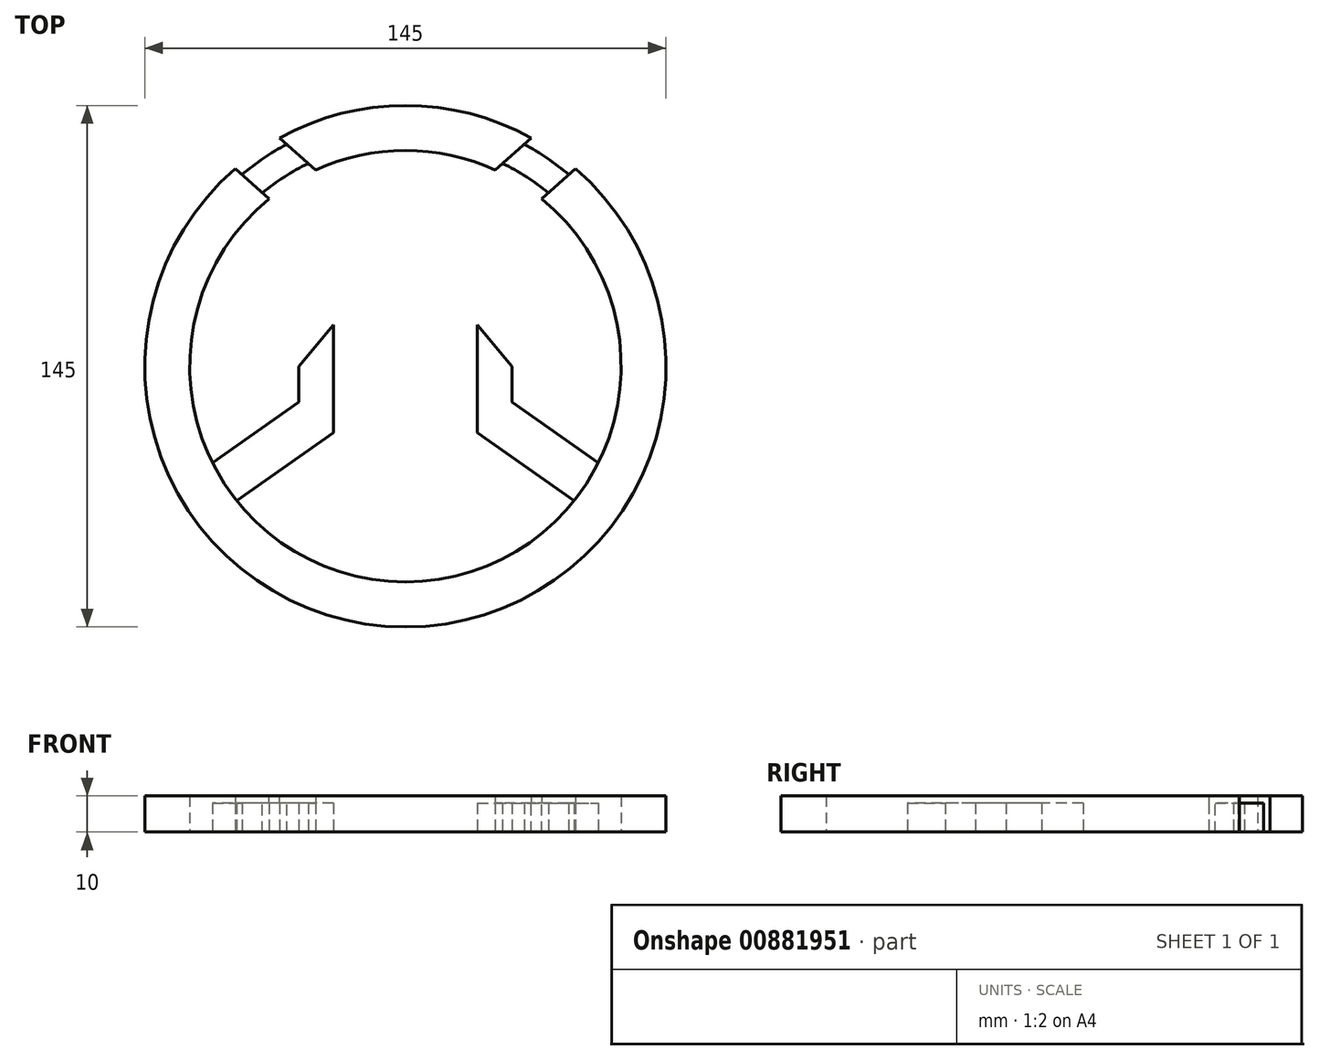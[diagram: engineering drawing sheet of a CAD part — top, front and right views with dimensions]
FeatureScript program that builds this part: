
annotation { "Feature Type Name" : "Feature", "Feature Type Description" : "" }
export const myFeature = defineFeature(function(context is Context, id is Id, definition is map)
    precondition{}
    {
        {
            var Q0;
            Q0=qCreatedBy(makeId("Top.planeOp"),FACE);
            var sketch = newSketch(context, id + "F0", { "sketchPlane" : qUnion([Q0])});
            skCircle(sketch, "E0", {"center": v(0, 0) * mm, "radius": 14 * mm});
            skArc(sketch, "E1", {"start": v(-20, -10.3) * mm, "mid": v(0, -22.5) * mm, "end": v(20, -10.3) * mm});
            skArc(sketch, "E2.MirrorC", {"start": v(20, -10.3) * mm, "mid": v(0, -22.5) * mm, "end": v(-20, -10.3) * mm});
            skLineSegment(sketch, "E3.right", {"start": v(-20, 11.5) * mm, "end": v(-20, -18.5) * mm});
            skPoint(sketch, "E4.orphan", {"position": v(0, 39.65) * mm});
            skLineSegment(sketch, "E5", {"start": v(-20, 11.5) * mm, "end": v(-29.64, 0) * mm});
            skLineSegment(sketch, "E6", {"start": v(-29.64, 0) * mm, "end": v(-29.64, -10) * mm});
            skLineSegment(sketch, "E7", {"start": v(-20, -18.5) * mm, "end": v(-46.94, -37.37) * mm});
            skLineSegment(sketch, "E8", {"start": v(-29.64, -10) * mm, "end": v(-53.67, -26.82) * mm});
            skArc(sketch, "E9", {"start": v(-46.94, -37.37) * mm, "mid": v(-26.05, -54.05) * mm, "end": v(0, -60) * mm});
            skArc(sketch, "E10", {"start": v(0, 72.5) * mm, "mid": v(-18.07, 70.21) * mm, "end": v(-35, 63.5) * mm});
            skArc(sketch, "E11.trimOffspring", {"start": v(0, 60) * mm, "mid": v(-12.8, 58.62) * mm, "end": v(-25, 54.54) * mm});
            skLineSegment(sketch, "E12.trimOffspring", {"start": v(0, 20) * mm, "end": v(0, 14) * mm});
            skLineSegment(sketch, "E13.trimOffspring", {"start": v(0, -14) * mm, "end": v(0, -20) * mm});
            skArc(sketch, "E14.MirrorCS", {"start": v(0, 72.5) * mm, "mid": v(18.07, 70.21) * mm, "end": v(35, 63.5) * mm});
            skArc(sketch, "E15.MirrorCS", {"start": v(0, 60) * mm, "mid": v(12.8, 58.62) * mm, "end": v(25, 54.54) * mm});
            skArc(sketch, "E16.MirrorCS", {"start": v(46.94, -37.37) * mm, "mid": v(26.05, -54.05) * mm, "end": v(0, -60) * mm});
            skLineSegment(sketch, "E17.MirrorCS", {"start": v(20, -18.5) * mm, "end": v(46.94, -37.37) * mm});
            skLineSegment(sketch, "E18.MirrorCS", {"start": v(29.64, -10) * mm, "end": v(53.67, -26.82) * mm});
            skLineSegment(sketch, "E19.MirrorCS", {"start": v(29.64, 0) * mm, "end": v(29.64, -10) * mm});
            skLineSegment(sketch, "E20.MirrorCS", {"start": v(20, 11.5) * mm, "end": v(29.64, 0) * mm});
            skLineSegment(sketch, "E21.MirrorCS", {"start": v(20, 11.5) * mm, "end": v(20, -18.5) * mm});
            skLineSegment(sketch, "E22", {"start": v(-35, 63.5) * mm, "end": v(-33.02, 61.72) * mm});
            skLineSegment(sketch, "E23.MirrorCS", {"start": v(35, 63.5) * mm, "end": v(33.02, 61.72) * mm});
            skLineSegment(sketch, "E24", {"start": v(-47.32, 54.93) * mm, "end": v(-45.44, 53.25) * mm});
            skLineSegment(sketch, "E25.MirrorCS", {"start": v(47.32, 54.93) * mm, "end": v(45.44, 53.25) * mm});
            skArc(sketch, "E26.trimOffspring", {"start": v(-47.32, 54.93) * mm, "mid": v(-67.97, -25.24) * mm, "end": v(0, -72.5) * mm});
            skArc(sketch, "E27.trimOffspring", {"start": v(-37.9, 46.5) * mm, "mid": v(-58.66, 12.6) * mm, "end": v(-53.67, -26.82) * mm});
            skArc(sketch, "E28.trimOffspring", {"start": v(37.9, 46.5) * mm, "mid": v(58.66, 12.6) * mm, "end": v(53.67, -26.82) * mm});
            skArc(sketch, "E29.trimOffspring", {"start": v(47.32, 54.93) * mm, "mid": v(67.97, -25.24) * mm, "end": v(0, -72.5) * mm});
            skArc(sketch, "E30", {"start": v(-27.02, 56.36) * mm, "mid": v(-33.66, 52.66) * mm, "end": v(-39.8, 48.2) * mm});
            skArc(sketch, "E31", {"start": v(-33.02, 61.72) * mm, "mid": v(-39.46, 57.82) * mm, "end": v(-45.44, 53.25) * mm});
            skArc(sketch, "E32.trimOffspring", {"start": v(45.44, 53.25) * mm, "mid": v(39.46, 57.82) * mm, "end": v(33.02, 61.72) * mm});
            skArc(sketch, "E33.trimOffspring", {"start": v(39.8, 48.2) * mm, "mid": v(33.66, 52.66) * mm, "end": v(27.02, 56.36) * mm});
            skLineSegment(sketch, "E34.trimOffspring", {"start": v(39.8, 48.2) * mm, "end": v(37.9, 46.5) * mm});
            skLineSegment(sketch, "E35.trimOffspring", {"start": v(27.02, 56.36) * mm, "end": v(25, 54.54) * mm});
            skLineSegment(sketch, "E36.trimOffspring", {"start": v(-27.02, 56.36) * mm, "end": v(-25, 54.54) * mm});
            skLineSegment(sketch, "E37.trimOffspring", {"start": v(-39.8, 48.2) * mm, "end": v(-37.9, 46.5) * mm});
            skArc(sketch, "E38.trimOffspring", {"start": v(20, 10.3) * mm, "mid": v(0, 22.5) * mm, "end": v(-20, 10.3) * mm});
            skArc(sketch, "E39.trimOffspring", {"start": v(-20, 10.3) * mm, "mid": v(0, 22.5) * mm, "end": v(20, 10.3) * mm});
            skSolve(sketch);
        }
        {
            var Q0;
            Q0 = qSketchRegion(id + "F0", true);
            var Q1;
            {var subQ3=sQuery(id+"F0.wireOp",EDGE,"E12.trimOffspring");Q1=makeQuery(id+"F0.imprint","IMPRINT",FACE,{"disambiguationData":[TD([[makeQuery(id+"F0.imprint","IMPRINT",EDGE,{"derivedFrom":subQ3}),-1.0]])]});}
            var Q2;
            {var subQ0=sQuery(id+"F0.wireOp",EDGE,"E12.trimOffspring");Q2=makeQuery(id+"F0.imprint","IMPRINT",FACE,{"disambiguationData":[TD([[makeQuery(id+"F0.imprint","IMPRINT",EDGE,{"derivedFrom":subQ0}),1.0]])]});}
            var Q3;
            {var subQ1=sQuery(id+"F0.wireOp",EDGE,"E2.MirrorC");Q3=makeQuery(id+"F0.imprint","IMPRINT",FACE,{"disambiguationData":[TD([[makeQuery(id+"F0.imprint","IMPRINT",EDGE,{"derivedFrom":subQ1}),-1.0]])]});}
            extrude(context, id + "F1", {"entities" : qUnion([Q0, Q1, Q2, Q3]), "depth" : 8 * mm, "offsetDistance" : 25 * mm});
        }
        {
            var Q0;
            Q0=qCreatedBy(makeId("Top.planeOp"),FACE);
            var sketch = newSketch(context, id + "F2", { "sketchPlane" : qUnion([Q0])});
            skArc(sketch, "E40", {"start": v(-37.9, 46.51) * mm, "mid": v(0, -60) * mm, "end": v(37.9, 46.51) * mm});
            skArc(sketch, "E41", {"start": v(-47.33, 54.92) * mm, "mid": v(0, -72.5) * mm, "end": v(47.33, 54.92) * mm});
            skLineSegment(sketch, "E42", {"start": v(-47.33, 54.92) * mm, "end": v(-37.9, 46.51) * mm});
            skLineSegment(sketch, "E43", {"start": v(-35, 63.5) * mm, "end": v(-24.99, 54.55) * mm});
            skLineSegment(sketch, "E44.MirrorCS", {"start": v(35, 63.5) * mm, "end": v(24.99, 54.55) * mm});
            skLineSegment(sketch, "E45.MirrorCS", {"start": v(47.33, 54.92) * mm, "end": v(37.9, 46.51) * mm});
            skArc(sketch, "E46.trimOffspring", {"start": v(24.99, 54.55) * mm, "mid": v(0, 60) * mm, "end": v(-24.99, 54.55) * mm});
            skArc(sketch, "E47.trimOffspring", {"start": v(35, 63.5) * mm, "mid": v(0, 72.5) * mm, "end": v(-35, 63.5) * mm});
            skSolve(sketch);
        }
        {
            var Q0;
            Q0 = qSketchRegion(id + "F2", true);
            extrude(context, id + "F3", {"entities" : qUnion([Q0]), "operationType" : NewBodyOperationType.ADD, "depth" : 10 * mm, "offsetDistance" : 25 * mm});
        }
    });
